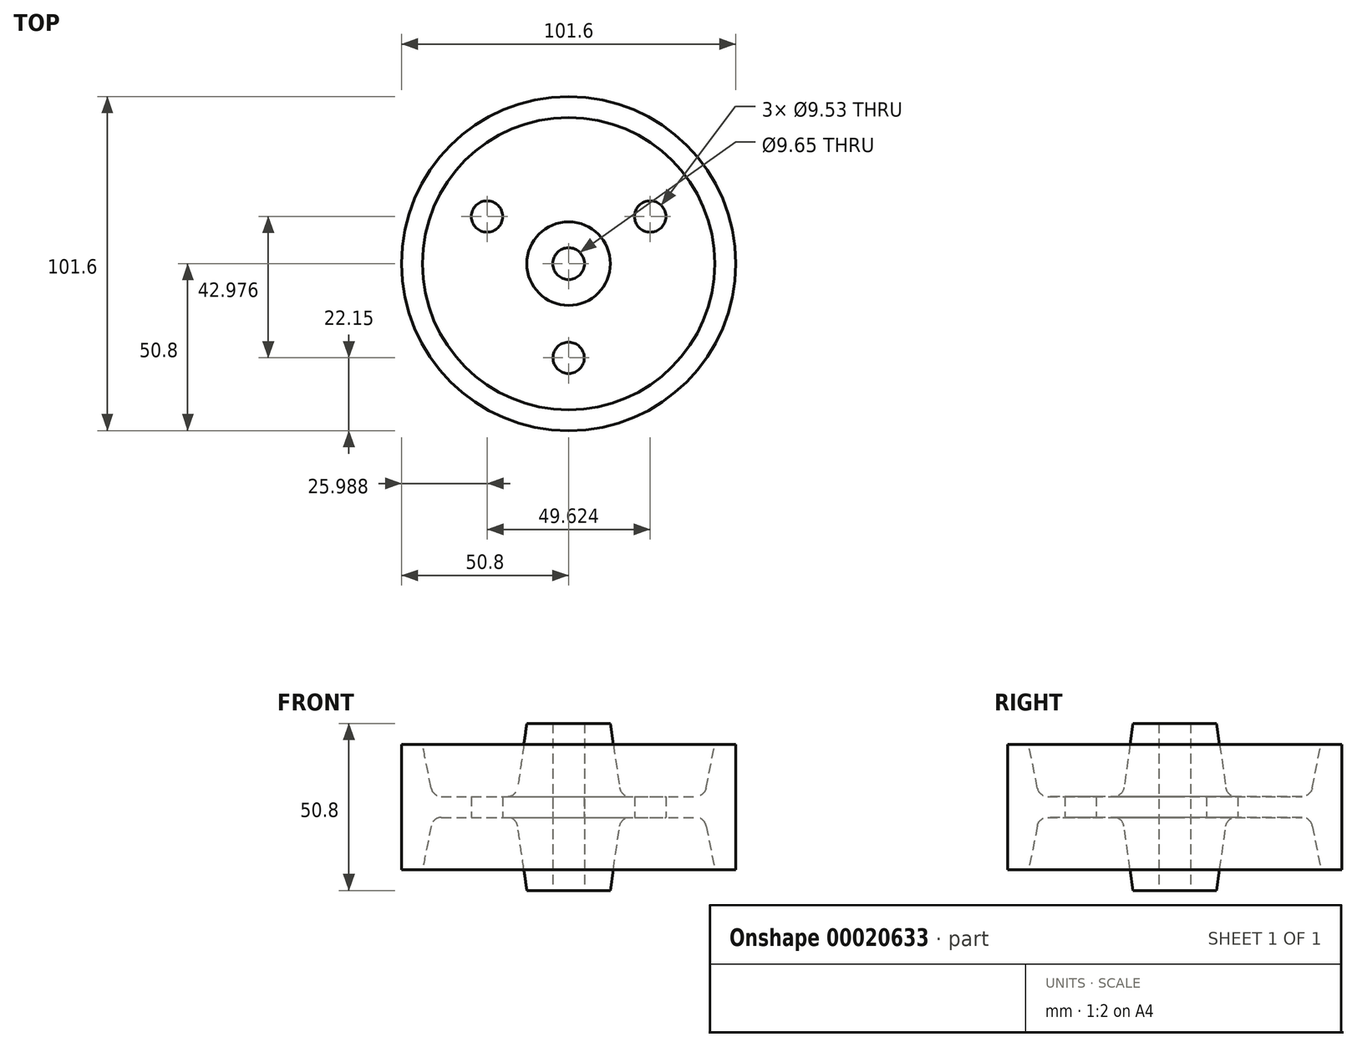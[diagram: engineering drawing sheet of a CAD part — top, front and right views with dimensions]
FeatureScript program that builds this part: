
annotation { "Feature Type Name" : "Feature", "Feature Type Description" : "" }
export const myFeature = defineFeature(function(context is Context, id is Id, definition is map)
    precondition{}
    {
        {
            var Q0;
            Q0=qCreatedBy(makeId("Front.planeOp"),FACE);
            var sketch = newSketch(context, id + "F0", { "sketchPlane" : qUnion([Q0])});
            skLineSegment(sketch, "E0", {"start": v(0, 0) * mm, "end": v(4.83, 0) * mm, "construction": true});
            skLineSegment(sketch, "E1", {"start": v(4.83, 0) * mm, "end": v(4.83, 25.4) * mm});
            skLineSegment(sketch, "E2", {"start": v(4.83, 0) * mm, "end": v(4.83, -25.4) * mm});
            skLineSegment(sketch, "E3", {"start": v(4.83, 25.4) * mm, "end": v(12.7, 25.4) * mm});
            skLineSegment(sketch, "E4", {"start": v(4.83, -25.4) * mm, "end": v(12.7, -25.4) * mm});
            skLineSegment(sketch, "E5", {"start": v(4.83, 0) * mm, "end": v(15.88, 0) * mm, "construction": true});
            skLineSegment(sketch, "E6", {"start": v(15.88, 0) * mm, "end": v(15.88, 3.18) * mm, "construction": true});
            skLineSegment(sketch, "E7", {"start": v(15.88, 0) * mm, "end": v(15.88, -3.18) * mm, "construction": true});
            skLineSegment(sketch, "E8", {"start": v(12.7, 25.4) * mm, "end": v(15.49, 5.9) * mm});
            skLineSegment(sketch, "E9", {"start": v(12.7, -25.4) * mm, "end": v(15.49, -5.9) * mm});
            skLineSegment(sketch, "E10", {"start": v(18.63, -3.18) * mm, "end": v(38.67, -3.18) * mm});
            skLineSegment(sketch, "E11", {"start": v(18.63, 3.18) * mm, "end": v(38.67, 3.18) * mm});
            skLineSegment(sketch, "E12", {"start": v(41.28, 3.18) * mm, "end": v(50.8, 3.18) * mm, "construction": true});
            skLineSegment(sketch, "E13", {"start": v(50.8, 0) * mm, "end": v(50.8, -19.05) * mm});
            skLineSegment(sketch, "E14", {"start": v(50.8, 0) * mm, "end": v(50.8, 19.05) * mm});
            skLineSegment(sketch, "E15", {"start": v(50.8, -19.05) * mm, "end": v(44.45, -19.05) * mm});
            skLineSegment(sketch, "E16", {"start": v(50.8, 19.05) * mm, "end": v(44.45, 19.05) * mm});
            skLineSegment(sketch, "E17", {"start": v(44.45, 19.05) * mm, "end": v(41.79, 5.73) * mm});
            skLineSegment(sketch, "E18", {"start": v(44.45, -19.05) * mm, "end": v(41.79, -5.73) * mm});
            skPoint(sketch, "E19.visualSharp", {"position": v(15.88, 3.18) * mm});
            skArc(sketch, "E19.filletArc", {"start": v(15.49, 5.9) * mm, "mid": v(16.55, 3.95) * mm, "end": v(18.63, 3.18) * mm});
            skPoint(sketch, "E20.visualSharp", {"position": v(15.88, -3.18) * mm});
            skArc(sketch, "E20.filletArc", {"start": v(18.63, -3.18) * mm, "mid": v(16.55, -3.95) * mm, "end": v(15.49, -5.9) * mm});
            skPoint(sketch, "E21.visualSharp", {"position": v(41.28, -3.18) * mm});
            skArc(sketch, "E21.filletArc", {"start": v(41.79, -5.73) * mm, "mid": v(40.69, -3.9) * mm, "end": v(38.67, -3.17) * mm});
            skPoint(sketch, "E22.visualSharp", {"position": v(41.28, 3.18) * mm});
            skArc(sketch, "E22.filletArc", {"start": v(38.67, 3.18) * mm, "mid": v(40.69, 3.9) * mm, "end": v(41.79, 5.73) * mm});
            skLineSegment(sketch, "E23", {"start": v(0, 0) * mm, "end": v(0, 2.76) * mm});
            skSolve(sketch);
        }
        {
            var Q0;
            Q0 = qSketchRegion(id + "F0", true);
            var Q1;
            Q1=sQuery(id+"F0.wireOp",EDGE,"E23");
            revolve(context, id + "F1", {"entities" : qUnion([Q0]), "axis" : qUnion([Q1]), "revolveType" : RevolveType.FULL});
        }
        {
            var Q0;
            Q0=makeQuery(id+"F1.opRevolve","SWEPT_FACE",FACE,{"disambiguationData":[OSD([sQuery(id+"F0.wireOp",EDGE,"E10")])]});
            var sketch = newSketch(context, id + "F2", { "sketchPlane" : qUnion([Q0])});
            skLineSegment(sketch, "E24", {"start": v(0, 18.63) * mm, "end": v(0, 38.67) * mm, "construction": true});
            skPoint(sketch, "E25", {"position": v(0, 28.65) * mm});
            skCircle(sketch, "E26", {"center": v(0, 28.65) * mm, "radius": 4.76 * mm});
            skCircle(sketch, "E27.1.0", {"center": v(-24.81, -14.33) * mm, "radius": 4.76 * mm});
            skCircle(sketch, "E27.2.0", {"center": v(24.81, -14.33) * mm, "radius": 4.76 * mm});
            skPoint(sketch, "E27.center", {"position": v(0, 0) * mm});
            skSolve(sketch);
        }
        {
            var Q0;
            Q0=sQuery(id+"F2.wireOp",VERTEX,"E25");
            var Q1;
            Q1=makeQuery(id+"F1.opRevolve","SWEPT_BODY",BODY,{"disambiguationData":[OSD([sQuery(id+"F0.wireOp",EDGE,"E1"),sQuery(id+"F0.wireOp",EDGE,"E2"),sQuery(id+"F0.wireOp",EDGE,"E3"),sQuery(id+"F0.wireOp",EDGE,"E4"),sQuery(id+"F0.wireOp",EDGE,"E8"),sQuery(id+"F0.wireOp",EDGE,"E9"),sQuery(id+"F0.wireOp",EDGE,"E10"),sQuery(id+"F0.wireOp",EDGE,"E11"),sQuery(id+"F0.wireOp",EDGE,"E13"),sQuery(id+"F0.wireOp",EDGE,"E14"),sQuery(id+"F0.wireOp",EDGE,"E15"),sQuery(id+"F0.wireOp",EDGE,"E16"),sQuery(id+"F0.wireOp",EDGE,"E17"),sQuery(id+"F0.wireOp",EDGE,"E18"),sQuery(id+"F0.wireOp",EDGE,"E19.filletArc"),sQuery(id+"F0.wireOp",EDGE,"E20.filletArc"),sQuery(id+"F0.wireOp",EDGE,"E21.filletArc"),sQuery(id+"F0.wireOp",EDGE,"E22.filletArc")])]});
            hole(context, id + "F3", {"style" : HoleStyle.SIMPLE, "holeDiameter" : 9.52 * mm, "endStyle" : HoleEndStyle.THROUGH, "locations" : qUnion([Q0]), "scope" : qUnion([Q1])});
        }
        {
            var Q0;
            Q0=sQuery(id+"F2.wireOp",VERTEX,"E27.1.0.center");
            var Q1;
            Q1=sQuery(id+"F2.wireOp",VERTEX,"E27.2.0.center");
            var Q2;
            Q2=makeQuery(id+"F1.opRevolve","SWEPT_BODY",BODY,{"disambiguationData":[OSD([sQuery(id+"F0.wireOp",EDGE,"E1"),sQuery(id+"F0.wireOp",EDGE,"E2"),sQuery(id+"F0.wireOp",EDGE,"E3"),sQuery(id+"F0.wireOp",EDGE,"E4"),sQuery(id+"F0.wireOp",EDGE,"E8"),sQuery(id+"F0.wireOp",EDGE,"E9"),sQuery(id+"F0.wireOp",EDGE,"E10"),sQuery(id+"F0.wireOp",EDGE,"E11"),sQuery(id+"F0.wireOp",EDGE,"E13"),sQuery(id+"F0.wireOp",EDGE,"E14"),sQuery(id+"F0.wireOp",EDGE,"E15"),sQuery(id+"F0.wireOp",EDGE,"E16"),sQuery(id+"F0.wireOp",EDGE,"E17"),sQuery(id+"F0.wireOp",EDGE,"E18"),sQuery(id+"F0.wireOp",EDGE,"E19.filletArc"),sQuery(id+"F0.wireOp",EDGE,"E20.filletArc"),sQuery(id+"F0.wireOp",EDGE,"E21.filletArc"),sQuery(id+"F0.wireOp",EDGE,"E22.filletArc")])]});
            hole(context, id + "F4", {"style" : HoleStyle.SIMPLE, "holeDiameter" : 9.52 * mm, "endStyle" : HoleEndStyle.THROUGH, "locations" : qUnion([Q0, Q1]), "scope" : qUnion([Q2])});
        }
    });
